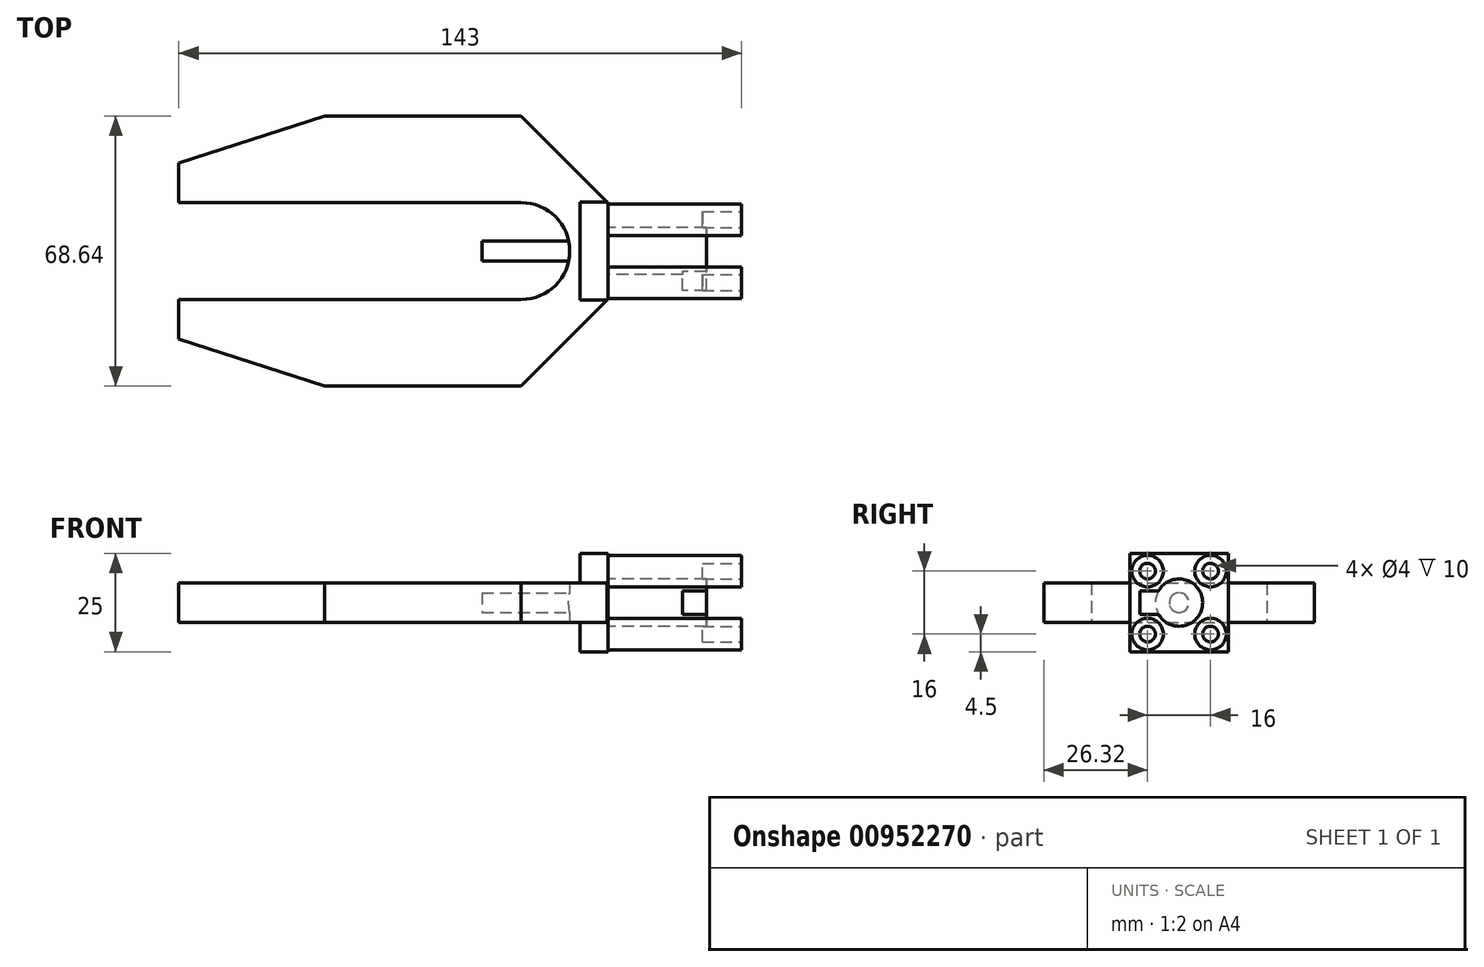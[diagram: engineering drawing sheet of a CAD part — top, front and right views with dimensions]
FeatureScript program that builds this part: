
annotation { "Feature Type Name" : "Feature", "Feature Type Description" : "" }
export const myFeature = defineFeature(function(context is Context, id is Id, definition is map)
    precondition{}
    {
        {
            var Q0;
            Q0=qCreatedBy(makeId("Top.planeOp"),FACE);
            var sketch = newSketch(context, id + "F0", { "sketchPlane" : qUnion([Q0])});
            skLineSegment(sketch, "E0.bottom", {"start": v(-50, 34.32) * mm, "end": v(0, 34.32) * mm});
            skLineSegment(sketch, "E0.top", {"start": v(-50, 12.32) * mm, "end": v(0, 12.32) * mm});
            skLineSegment(sketch, "E0.left", {"start": v(0, 34.32) * mm, "end": v(0, 12.32) * mm});
            skLineSegment(sketch, "E0.right", {"start": v(-50, 34.32) * mm, "end": v(-50, 12.32) * mm});
            skLineSegment(sketch, "E1", {"start": v(22, 12.32) * mm, "end": v(0, 34.32) * mm});
            skLineSegment(sketch, "E2", {"start": v(-50, 12.32) * mm, "end": v(-87, 12.32) * mm});
            skLineSegment(sketch, "E3", {"start": v(-87, 12.32) * mm, "end": v(-87, 22.32) * mm});
            skLineSegment(sketch, "E4", {"start": v(-87, 22.32) * mm, "end": v(-50, 34.32) * mm});
            skLineSegment(sketch, "E5", {"start": v(22, 0) * mm, "end": v(12.32, 0) * mm});
            skLineSegment(sketch, "E6", {"start": v(0, 12.32) * mm, "end": v(22, 12.32) * mm});
            skLineSegment(sketch, "E7", {"start": v(22, 12.32) * mm, "end": v(22, 0) * mm});
            skArc(sketch, "E8", {"start": v(12.32, 0) * mm, "mid": v(8.7, 8.7) * mm, "end": v(0, 12.32) * mm});
            skLineSegment(sketch, "E9.MirrorCS", {"start": v(-50, -12.32) * mm, "end": v(0, -12.32) * mm});
            skLineSegment(sketch, "E10.MirrorCS", {"start": v(0, -12.32) * mm, "end": v(22, -12.32) * mm});
            skArc(sketch, "E11.MirrorCS", {"start": v(12.32, 0) * mm, "mid": v(8.7, -8.7) * mm, "end": v(0, -12.32) * mm});
            skLineSegment(sketch, "E12.MirrorCS", {"start": v(22, -12.32) * mm, "end": v(0, -34.32) * mm});
            skLineSegment(sketch, "E13.MirrorCS", {"start": v(-50, -34.32) * mm, "end": v(0, -34.32) * mm});
            skLineSegment(sketch, "E14.MirrorCS", {"start": v(-87, -22.32) * mm, "end": v(-50, -34.32) * mm});
            skLineSegment(sketch, "E15.MirrorCS", {"start": v(-87, -12.32) * mm, "end": v(-87, -22.32) * mm});
            skLineSegment(sketch, "E16.MirrorCS", {"start": v(-50, -12.32) * mm, "end": v(-87, -12.32) * mm});
            skLineSegment(sketch, "E17.MirrorCS", {"start": v(22, -12.32) * mm, "end": v(22, 0) * mm});
            skSolve(sketch);
        }
        {
            var Q0;
            Q0 = qSketchRegion(id + "F0", true);
            extrude(context, id + "F1", {"entities" : qUnion([Q0]), "depth" : 10 * mm, "offsetDistance" : 25 * mm, "symmetric" : true});
        }
        {
            var Q0;
            Q0=makeQuery(id+"F1.opExtrude","SWEPT_FACE",FACE,{"disambiguationData":[OSD([sQuery(id+"F0.wireOp",EDGE,"E7"),sQuery(id+"F0.wireOp",EDGE,"E17.MirrorCS")])]});
            var sketch = newSketch(context, id + "F2", { "sketchPlane" : qUnion([Q0])});
            skLineSegment(sketch, "E18.bottom", {"start": v(-12.5, -12.5) * mm, "end": v(12.5, -12.5) * mm});
            skLineSegment(sketch, "E18.top", {"start": v(-12.5, 12.5) * mm, "end": v(12.5, 12.5) * mm});
            skLineSegment(sketch, "E18.left", {"start": v(-12.5, -12.5) * mm, "end": v(-12.5, 12.5) * mm});
            skLineSegment(sketch, "E18.right", {"start": v(12.5, -12.5) * mm, "end": v(12.5, 12.5) * mm});
            skPoint(sketch, "E18.middle", {"position": v(0, 0) * mm});
            skSolve(sketch);
        }
        {
            var Q0;
            Q0 = qSketchRegion(id + "F2", true);
            extrude(context, id + "F3", {"entities" : qUnion([Q0]), "operationType" : NewBodyOperationType.ADD, "oppositeDirection" : true, "depth" : 7 * mm, "offsetDistance" : 25 * mm});
        }
        {
            var Q0;
            Q0=makeQuery(id+"F3.boolean.opBoolean","MERGE",FACE,{"derivedFrom":[makeQuery(id+"F1.opExtrude","SWEPT_FACE",FACE,{"disambiguationData":[OSD([sQuery(id+"F0.wireOp",EDGE,"E7"),sQuery(id+"F0.wireOp",EDGE,"E17.MirrorCS")])]}),makeQuery(id+"F3.opExtrude","CAP_FACE",FACE,{"disambiguationData":[OSD([sQuery(id+"F2.wireOp",EDGE,"E18.bottom"),sQuery(id+"F2.wireOp",EDGE,"E18.top"),sQuery(id+"F2.wireOp",EDGE,"E18.left"),sQuery(id+"F2.wireOp",EDGE,"E18.right")])],"isStart":true})]});
            var sketch = newSketch(context, id + "F4", { "sketchPlane" : qUnion([Q0])});
            skCircle(sketch, "E19", {"center": v(0, 0) * mm, "radius": 6 * mm});
            skSolve(sketch);
        }
        {
            var Q0;
            Q0 = qSketchRegion(id + "F4", true);
            extrude(context, id + "F5", {"entities" : qUnion([Q0]), "operationType" : NewBodyOperationType.ADD, "depth" : 25 * mm, "offsetDistance" : 25 * mm});
        }
        {
            var Q0;
            Q0=makeQuery(id+"F3.boolean.opBoolean","MERGE",FACE,{"derivedFrom":[makeQuery(id+"F1.opExtrude","SWEPT_FACE",FACE,{"disambiguationData":[OSD([sQuery(id+"F0.wireOp",EDGE,"E7"),sQuery(id+"F0.wireOp",EDGE,"E17.MirrorCS")])]}),makeQuery(id+"F3.opExtrude","CAP_FACE",FACE,{"disambiguationData":[OSD([sQuery(id+"F2.wireOp",EDGE,"E18.bottom"),sQuery(id+"F2.wireOp",EDGE,"E18.top"),sQuery(id+"F2.wireOp",EDGE,"E18.left"),sQuery(id+"F2.wireOp",EDGE,"E18.right")])],"isStart":true})]});
            var sketch = newSketch(context, id + "F6", { "sketchPlane" : qUnion([Q0])});
            skCircle(sketch, "E20", {"center": v(8, 8) * mm, "radius": 4 * mm});
            skCircle(sketch, "E21.MirrorC", {"center": v(-8, 8) * mm, "radius": 4 * mm});
            skCircle(sketch, "E22.MirrorC", {"center": v(8, -8) * mm, "radius": 4 * mm});
            skCircle(sketch, "E23.MirrorC", {"center": v(-8, -8) * mm, "radius": 4 * mm});
            skSolve(sketch);
        }
        {
            var Q0;
            Q0 = qSketchRegion(id + "F6", true);
            extrude(context, id + "F7", {"entities" : qUnion([Q0]), "operationType" : NewBodyOperationType.ADD, "depth" : 34 * mm, "offsetDistance" : 25 * mm});
        }
        {
            var Q0;
            Q0=makeQuery(id+"F7.opExtrude","CAP_FACE",FACE,{"disambiguationData":[OSD([sQuery(id+"F6.wireOp",EDGE,"E20")])],"isStart":false});
            var sketch = newSketch(context, id + "F8", { "sketchPlane" : qUnion([Q0])});
            skCircle(sketch, "E24", {"center": v(8, 8) * mm, "radius": 2 * mm});
            skCircle(sketch, "E25.MirrorC", {"center": v(-8, 8) * mm, "radius": 2 * mm});
            skCircle(sketch, "E26.MirrorC", {"center": v(8, -8) * mm, "radius": 2 * mm});
            skCircle(sketch, "E27.MirrorC", {"center": v(-8, -8) * mm, "radius": 2 * mm});
            skSolve(sketch);
        }
        {
            var Q0;
            Q0 = qSketchRegion(id + "F8", true);
            extrude(context, id + "F9", {"entities" : qUnion([Q0]), "operationType" : NewBodyOperationType.REMOVE, "oppositeDirection" : true, "depth" : 10 * mm, "offsetDistance" : 25 * mm});
        }
        {
            var Q0;
            {var subQ0=sQuery(id+"F2.wireOp",EDGE,"E18.left");var subQ1=sQuery(id+"F2.wireOp",EDGE,"E18.top");var subQ2=sQuery(id+"F2.wireOp",EDGE,"E18.right");Q0=makeQuery(id+"F3.boolean.opBoolean","SPLIT",FACE,{"disambiguationData":[TD([makeQuery(id+"F3.opExtrude","SWEPT_FACE",FACE,{"disambiguationData":[OSD([subQ1])]})])],"derivedFrom":makeQuery(id+"F3.opExtrude","CAP_FACE",FACE,{"disambiguationData":[OSD([sQuery(id+"F2.wireOp",EDGE,"E18.bottom"),subQ1,subQ0,subQ2])],"isStart":false})});}
            var sketch = newSketch(context, id + "F10", { "sketchPlane" : qUnion([Q0])});
            skCircle(sketch, "E28", {"center": v(0, 0) * mm, "radius": 2.5 * mm});
            skSolve(sketch);
        }
        {
            var Q0;
            Q0 = qSketchRegion(id + "F10", true);
            extrude(context, id + "F11", {"entities" : qUnion([Q0]), "operationType" : NewBodyOperationType.ADD, "depth" : 25 * mm, "offsetDistance" : 25 * mm});
        }
        {
            var Q0;
            Q0=qCreatedBy(makeId("Front.planeOp"),FACE);
            var sketch = newSketch(context, id + "F12", { "sketchPlane" : qUnion([Q0])});
            skLineSegment(sketch, "E29.bottom", {"start": v(47, 3) * mm, "end": v(41, 3) * mm});
            skLineSegment(sketch, "E29.top", {"start": v(47, -3) * mm, "end": v(41, -3) * mm});
            skLineSegment(sketch, "E29.left", {"start": v(47, 3) * mm, "end": v(47, -3) * mm});
            skLineSegment(sketch, "E29.right", {"start": v(41, 3) * mm, "end": v(41, -3) * mm});
            skSolve(sketch);
        }
        {
            var Q0;
            Q0 = qSketchRegion(id + "F12", true);
            extrude(context, id + "F13", {"entities" : qUnion([Q0]), "operationType" : NewBodyOperationType.ADD, "depth" : 10 * mm, "offsetDistance" : 25 * mm});
        }
    });
